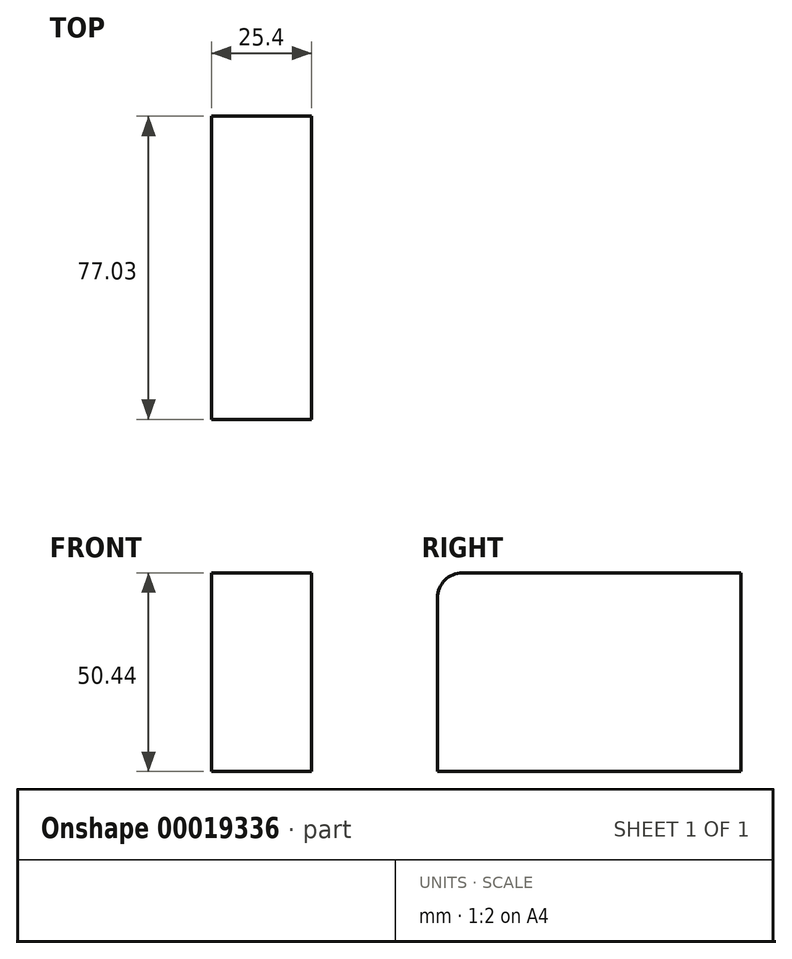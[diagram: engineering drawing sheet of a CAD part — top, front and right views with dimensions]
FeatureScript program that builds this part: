
annotation { "Feature Type Name" : "Feature", "Feature Type Description" : "" }
export const myFeature = defineFeature(function(context is Context, id is Id, definition is map)
    precondition{}
    {
        {
            var Q0;
            Q0=qCreatedBy(makeId("Right.planeOp"),FACE);
            var sketch = newSketch(context, id + "F0", { "sketchPlane" : qUnion([Q0])});
            skLineSegment(sketch, "E0.bottom", {"start": v(-26.08, 20) * mm, "end": v(44.6, 20) * mm});
            skLineSegment(sketch, "E0.top", {"start": v(-32.43, -30.44) * mm, "end": v(44.6, -30.44) * mm});
            skLineSegment(sketch, "E0.left", {"start": v(-32.43, 13.65) * mm, "end": v(-32.43, -30.44) * mm});
            skLineSegment(sketch, "E0.right", {"start": v(44.6, 20) * mm, "end": v(44.6, -30.44) * mm});
            skPoint(sketch, "E1.visualSharp", {"position": v(-32.43, 20) * mm});
            skArc(sketch, "E1.filletArc", {"start": v(-26.08, 20) * mm, "mid": v(-30.57, 18.14) * mm, "end": v(-32.43, 13.65) * mm});
            skSolve(sketch);
        }
        {
            var Q0;
            Q0 = qSketchRegion(id + "F0", true);
            extrude(context, id + "F1", {"entities" : qUnion([Q0]), "depth" : 25.4 * mm, "offsetDistance" : 25.4 * mm});
        }
    });
